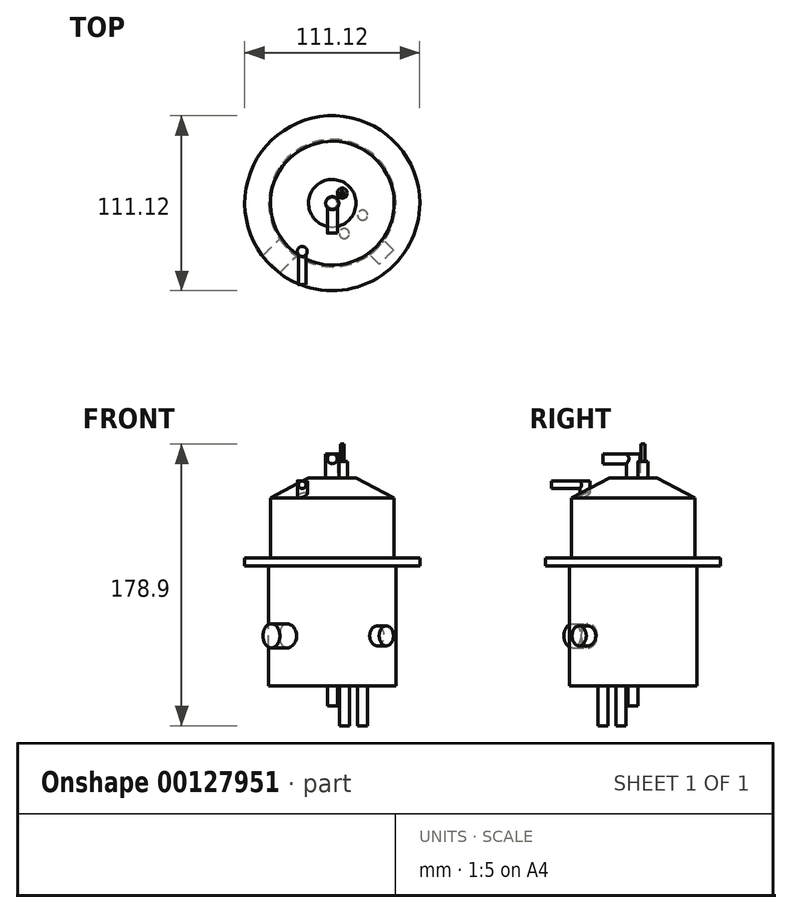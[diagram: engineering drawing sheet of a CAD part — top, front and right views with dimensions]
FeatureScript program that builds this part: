
annotation { "Feature Type Name" : "Feature", "Feature Type Description" : "" }
export const myFeature = defineFeature(function(context is Context, id is Id, definition is map)
    precondition{}
    {
        {
            var Q0;
            Q0=qCreatedBy(makeId("Top.planeOp"),FACE);
            var sketch = newSketch(context, id + "F0", { "sketchPlane" : qUnion([Q0])});
            skCircle(sketch, "E0", {"center": v(0, 0) * mm, "radius": 40.48 * mm});
            skSolve(sketch);
        }
        {
            var Q0;
            Q0=makeQuery(id+"F0.imprint","IMPRINT",FACE,{"disambiguationData":[TD([[makeQuery(id+"F0.imprint","IMPRINT",EDGE,{"derivedFrom":sQuery(id+"F0.wireOp",EDGE,"E0")}),1.0]])]});
            extrude(context, id + "F1", {"entities" : qUnion([Q0]), "oppositeDirection" : true, "depth" : 76.2 * mm});
        }
        {
            var Q0;
            Q0=makeQuery(id+"F1.opExtrude","CAP_FACE",FACE,{"disambiguationData":[OSD([sQuery(id+"F0.wireOp",EDGE,"E0")])],"isStart":true});
            var sketch = newSketch(context, id + "F2", { "sketchPlane" : qUnion([Q0])});
            skCircle(sketch, "E1", {"center": v(0, 0) * mm, "radius": 55.56 * mm});
            skSolve(sketch);
        }
        {
            var Q0;
            Q0 = qSketchRegion(id + "F2", true);
            extrude(context, id + "F3", {"entities" : qUnion([Q0]), "operationType" : NewBodyOperationType.ADD, "depth" : 5.16 * mm});
        }
        {
            var Q0;
            Q0=makeQuery(id+"F3.opExtrude","CAP_FACE",FACE,{"disambiguationData":[OSD([sQuery(id+"F2.wireOp",EDGE,"E1")])],"isStart":false});
            var sketch = newSketch(context, id + "F4", { "sketchPlane" : qUnion([Q0])});
            skCircle(sketch, "E2", {"center": v(0, 0) * mm, "radius": 39.3 * mm});
            skSolve(sketch);
        }
        {
            var Q0;
            Q0=makeQuery(id+"F4.imprint","IMPRINT",FACE,{"disambiguationData":[TD([[makeQuery(id+"F4.imprint","IMPRINT",EDGE,{"derivedFrom":sQuery(id+"F4.wireOp",EDGE,"E2")}),1.0]])]});
            extrude(context, id + "F5", {"entities" : qUnion([Q0]), "operationType" : NewBodyOperationType.ADD, "depth" : 38.1 * mm});
        }
        {
            var Q0;
            Q0=qCreatedBy(makeId("Front.planeOp"),FACE);
            var sketch = newSketch(context, id + "F6", { "sketchPlane" : qUnion([Q0])});
            skLineSegment(sketch, "E3", {"start": v(0, 55.96) * mm, "end": v(15.08, 55.96) * mm});
            skLineSegment(sketch, "E4.0", {"start": v(0, 43.26) * mm, "end": v(39.3, 43.26) * mm});
            skLineSegment(sketch, "E5", {"start": v(15.08, 55.96) * mm, "end": v(39.3, 43.26) * mm});
            skLineSegment(sketch, "E6", {"start": v(0, 55.96) * mm, "end": v(0, 43.26) * mm});
            skSolve(sketch);
        }
        {
            var Q0;
            Q0=makeQuery(id+"F6.imprint","IMPRINT",FACE,{"disambiguationData":[TD([[makeQuery(id+"F6.imprint","IMPRINT",EDGE,{"derivedFrom":sQuery(id+"F6.wireOp",EDGE,"E3")}),-1.0]])]});
            var Q1;
            Q1=sQuery(id+"F6.wireOp",EDGE,"E6");
            revolve(context, id + "F7", {"operationType" : NewBodyOperationType.ADD, "entities" : qUnion([Q0]), "axis" : qUnion([Q1]), "revolveType" : RevolveType.FULL});
        }
        {
            var Q0;
            Q0=qCreatedBy(makeId("Front.planeOp"),FACE);
            var Q1;
            Q1=qCreatedBy(makeId("Right.planeOp"),FACE);
            cPlane(context, id + "F8", {"entities" : qUnion([Q0, Q1]), "cplaneType" : CPlaneType.MID_PLANE, "offset" : 25.4 * mm, "width" : 152.4 * mm, "height" : 152.4 * mm});
        }
        {
            var Q0;
            Q0=qCreatedBy(makeId("Right.planeOp"),FACE);
            var Q1;
            Q1=qCreatedBy(makeId("Front.planeOp"),FACE);
            cPlane(context, id + "F9", {"entities" : qUnion([Q0, Q1]), "cplaneType" : CPlaneType.MID_PLANE, "offset" : 25.4 * mm, "flipAlignment" : true, "width" : 152.4 * mm, "height" : 152.4 * mm});
        }
        {
            var Q0;
            Q0=qCreatedBy(id+"F8.planeOp",FACE);
            var sketch = newSketch(context, id + "F10", { "sketchPlane" : qUnion([Q0])});
            skCircle(sketch, "E7", {"center": v(0, -44.45) * mm, "radius": 7.62 * mm});
            skSolve(sketch);
        }
        {
            var Q0;
            Q0 = qSketchRegion(id + "F10", true);
            extrude(context, id + "F11", {"entities" : qUnion([Q0]), "operationType" : NewBodyOperationType.ADD, "depth" : 54.6 * mm});
        }
        {
            var Q0;
            Q0=qCreatedBy(id+"F9.planeOp",FACE);
            var sketch = newSketch(context, id + "F12", { "sketchPlane" : qUnion([Q0])});
            skCircle(sketch, "E8", {"center": v(0, -44.45) * mm, "radius": 6.35 * mm});
            skSolve(sketch);
        }
        {
            var Q0;
            Q0 = qSketchRegion(id + "F12", true);
            extrude(context, id + "F13", {"entities" : qUnion([Q0]), "operationType" : NewBodyOperationType.ADD, "depth" : 48.5 * mm});
        }
        {
            var Q0;
            Q0=makeQuery(id+"F1.opExtrude","CAP_FACE",FACE,{"disambiguationData":[OSD([sQuery(id+"F0.wireOp",EDGE,"E0")])],"isStart":false});
            var sketch = newSketch(context, id + "F14", { "sketchPlane" : qUnion([Q0])});
            skCircle(sketch, "E9", {"center": v(0, 0) * mm, "radius": 3.18 * mm});
            skSolve(sketch);
        }
        {
            var Q0;
            Q0 = qSketchRegion(id + "F14", true);
            extrude(context, id + "F15", {"entities" : qUnion([Q0]), "operationType" : NewBodyOperationType.ADD, "depth" : 12.7 * mm});
        }
        {
            var Q0;
            Q0=makeQuery(id+"F1.opExtrude","CAP_FACE",FACE,{"disambiguationData":[OSD([sQuery(id+"F0.wireOp",EDGE,"E0")])],"isStart":false});
            var sketch = newSketch(context, id + "F16", { "sketchPlane" : qUnion([Q0])});
            skCircle(sketch, "E10", {"center": v(7.63, 19.3) * mm, "radius": 3.18 * mm});
            skCircle(sketch, "E11", {"center": v(19.3, 7.63) * mm, "radius": 3.18 * mm});
            skLineSegment(sketch, "E12", {"start": v(7.63, 19.3) * mm, "end": v(19.3, 7.63) * mm, "construction": true});
            skLineSegment(sketch, "E13", {"start": v(0, 0) * mm, "end": v(13.47, 13.47) * mm, "construction": true});
            skSolve(sketch);
        }
        {
            var Q0;
            Q0 = qSketchRegion(id + "F16", true);
            extrude(context, id + "F17", {"entities" : qUnion([Q0]), "operationType" : NewBodyOperationType.ADD, "depth" : 25.4 * mm});
        }
        {
            var Q0;
            Q0=makeQuery(id+"F7.opRevolve","SWEPT_FACE",FACE,{"disambiguationData":[OSD([sQuery(id+"F6.wireOp",EDGE,"E3")])]});
            var sketch = newSketch(context, id + "F18", { "sketchPlane" : qUnion([Q0])});
            skCircle(sketch, "E14", {"center": v(0, 0) * mm, "radius": 4.2 * mm});
            skSolve(sketch);
        }
        {
            var Q0;
            Q0=makeQuery(id+"F18.imprint","IMPRINT",FACE,{"disambiguationData":[TD([[makeQuery(id+"F18.imprint","IMPRINT",EDGE,{"derivedFrom":sQuery(id+"F18.wireOp",EDGE,"E14")}),1.0]])]});
            extrude(context, id + "F19", {"entities" : qUnion([Q0]), "operationType" : NewBodyOperationType.ADD, "depth" : 15.24 * mm});
        }
        {
            var Q0;
            Q0=qCreatedBy(makeId("Front.planeOp"),FACE);
            var sketch = newSketch(context, id + "F20", { "sketchPlane" : qUnion([Q0])});
            skCircle(sketch, "E15", {"center": v(0, 68.02) * mm, "radius": 3.18 * mm});
            skSolve(sketch);
        }
        {
            var Q0;
            Q0 = qSketchRegion(id + "F20", true);
            extrude(context, id + "F21", {"entities" : qUnion([Q0]), "operationType" : NewBodyOperationType.ADD, "depth" : 19.05 * mm});
        }
        {
            var Q0;
            Q0=makeQuery(id+"F7.opRevolve","SWEPT_FACE",FACE,{"disambiguationData":[OSD([sQuery(id+"F6.wireOp",EDGE,"E3")])]});
            var sketch = newSketch(context, id + "F22", { "sketchPlane" : qUnion([Q0])});
            skCircle(sketch, "E16", {"center": v(6.35, 6.35) * mm, "radius": 3.18 * mm});
            skSolve(sketch);
        }
        {
            var Q0;
            Q0 = qSketchRegion(id + "F22", true);
            extrude(context, id + "F23", {"entities" : qUnion([Q0]), "operationType" : NewBodyOperationType.ADD, "depth" : 10.4 * mm});
        }
        {
            var Q0;
            Q0=makeQuery(id+"F23.opExtrude","CAP_FACE",FACE,{"disambiguationData":[OSD([sQuery(id+"F22.wireOp",EDGE,"E16")])],"isStart":false});
            var sketch = newSketch(context, id + "F24", { "sketchPlane" : qUnion([Q0])});
            skCircle(sketch, "E17", {"center": v(6.35, 6.35) * mm, "radius": 1.27 * mm});
            skSolve(sketch);
        }
        {
            var Q0;
            Q0=makeQuery(id+"F24.imprint","IMPRINT",FACE,{"disambiguationData":[TD([[makeQuery(id+"F24.imprint","IMPRINT",EDGE,{"derivedFrom":sQuery(id+"F24.wireOp",EDGE,"E17")}),1.0]])]});
            extrude(context, id + "F25", {"entities" : qUnion([Q0]), "operationType" : NewBodyOperationType.ADD, "depth" : 10.92 * mm});
        }
        {
            var Q0;
            Q0=makeQuery(id+"F3.opExtrude","CAP_FACE",FACE,{"disambiguationData":[OSD([sQuery(id+"F2.wireOp",EDGE,"E1")])],"isStart":false});
            var sketch = newSketch(context, id + "F26", { "sketchPlane" : qUnion([Q0])});
            skCircle(sketch, "E18", {"center": v(-19.05, -30.68) * mm, "radius": 3.18 * mm});
            skSolve(sketch);
        }
        {
            var Q0;
            Q0 = qSketchRegion(id + "F26", true);
            extrude(context, id + "F27", {"entities" : qUnion([Q0]), "operationType" : NewBodyOperationType.ADD, "depth" : 48.77 * mm});
        }
        {
            var Q0;
            Q0=makeQuery(id+"F27.opExtrude","CAP_FACE",FACE,{"disambiguationData":[OSD([sQuery(id+"F26.wireOp",EDGE,"E18")])],"isStart":false});
            var sketch = newSketch(context, id + "F28", { "sketchPlane" : qUnion([Q0])});
            skPoint(sketch, "E19", {"position": v(-19.05, -30.68) * mm});
            skSolve(sketch);
        }
        {
            var Q0;
            Q0=qCreatedBy(makeId("Front.planeOp"),FACE);
            var Q1;
            Q1=sQuery(id+"F28.wireOp",VERTEX,"E19");
            cPlane(context, id + "F29", {"entities" : qUnion([Q0, Q1]), "cplaneType" : CPlaneType.PLANE_POINT, "offset" : 25.4 * mm, "width" : 152.4 * mm, "height" : 152.4 * mm});
        }
        {
            var Q0;
            Q0=qCreatedBy(id+"F29.planeOp",FACE);
            var sketch = newSketch(context, id + "F30", { "sketchPlane" : qUnion([Q0])});
            skCircle(sketch, "E20", {"center": v(-19.05, 51.51) * mm, "radius": 2.41 * mm});
            skSolve(sketch);
        }
        {
            var Q0;
            Q0 = qSketchRegion(id + "F30", true);
            extrude(context, id + "F31", {"entities" : qUnion([Q0]), "operationType" : NewBodyOperationType.ADD, "depth" : 21.08 * mm});
        }
    });
